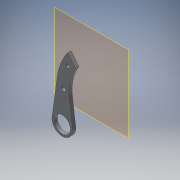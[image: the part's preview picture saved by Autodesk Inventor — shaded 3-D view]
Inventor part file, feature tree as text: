
AUTODESK INVENTOR PART (.ipt)
format: ipt  version: 2019.3 (Build 233278000, 278)  size: 114,176 bytes
history: native  units: mm
features: other x3, reference x2, plane x1, extrude x1, sketch x1
ambient origin geometry x8: Origin, YZ Plane, XZ Plane, XY Plane, X Axis, Y Axis, Z Axis, Center Point
bodies: Solid1 (feature_tree)
feature tree (8):
  plane  "Work Plane1"
  extrude  "Extrusion1"  [1 undecoded]
  sketch  "Sketch1"  dims[d0=4.4mm d1=0.0mm]
  reference  "Reference2"
  reference  "Reference4"
  other  "<userpath>\Desktop\3dprojects\OpenEmoto\Swingarm3\Swingarm3.iam"
  other  "Swingarm3.iam"
  other  "FrontMotorPlateBridge:1"
note: 1 required parameter value undecoded (feature->parameter linkage not recoverable at this tier; creation-order binding heuristic only, values carry confidence <= 0.55)
